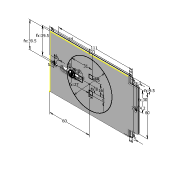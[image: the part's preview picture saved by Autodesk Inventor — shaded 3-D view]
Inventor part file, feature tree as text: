
AUTODESK INVENTOR PART (.ipt)
format: ipt  version: 2022 (Build 260153000, 153)  size: 190,464 bytes
history: native  units: mm
features: extrude x9, sketch x6, fillet x3
ambient origin geometry x8: Origin, YZ Plane, XZ Plane, XY Plane, X Axis, Y Axis, Z Axis, Center Point
bodies: Solid1 (feature_tree)
feature tree (18):
  sketch  "Sketch1"  dims[d0=123.0mm d1=79.0mm]
  extrude  "Extrusion1"  Depth=79.0mm
  extrude  "Extrusion3"  Depth=3.5mm
  sketch  "Sketch2"  dims[d2=111.0mm d3=3.5mm]
  extrude  "Extrusion4"  Depth=60.0mm
  sketch  "Sketch3"  dims[d4=6.0mm d5=60.0mm]
  extrude  "Extrusion5"  Depth=4.0mm
  fillet  "Fillet1"  Radius=4.0mm
  extrude  "Extrusion6"  Depth=3.0mm
  extrude  "Extrusion7"  Depth=2.0mm TaperAngle=0.0deg
  fillet  "Fillet2"  Radius=2.0mm
  extrude  "Extrusion8"  Depth=5.0mm
  fillet  "Fillet3"  Radius=3.0mm
  sketch  "Sketch5"  dims[d9=4.2mm d10=3.0mm]
  extrude  "Extrusion9"  Depth=4.0mm
  extrude  "Extrusion10"  Depth=8.0mm
  sketch  "Sketch4"  dims[d6=9.5mm d7=4.0mm d8=4.0mm]
  sketch  "Sketch6"  dims[d11=30.0mm d12=2.0mm d13=0.0mm d16=2.0mm d17=0.0mm d20=5.0mm d21=3.0mm d22=4.0mm d23=39.5mm d24=68.0mm d25=39.5mm d26=60.0mm d27=16.0mm d28=5.0mm d29=5.0mm d30=8.0mm d31=5.0mm d32=31.0mm d33=27.0mm d34=3.0mm d35=8.0mm d36=64.0mm d37=2.0mm d38=10.0mm d39=3.7mm d40=0.0mm d41=1.1mm d42=1.1mm d43=1.3mm d44=0.0mm d45=0.25mm d46=4.5mm d47=0.0mm d48=2.0mm d49=0.0mm d50=1.0mm d51=16.0mm d52=6.928203mm d53=0.0mm d54=0.0mm d55=1.0mm d56=0.0mm d57=0.0mm d58=8.0mm d59=20.0mm d60=20.0mm d61=0.0mm d62=0.0mm]
